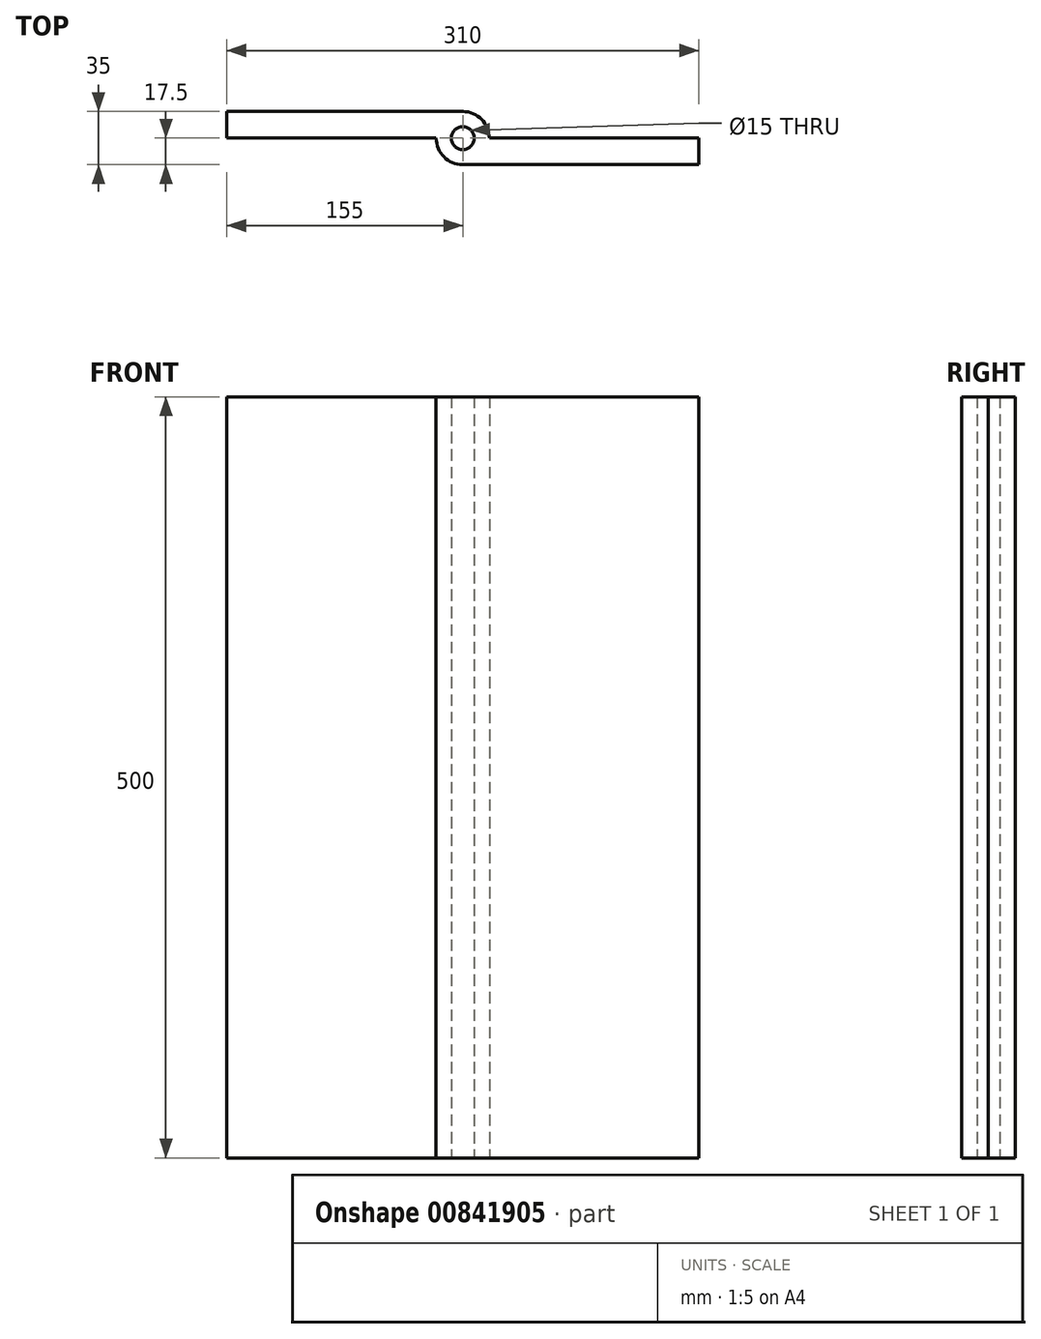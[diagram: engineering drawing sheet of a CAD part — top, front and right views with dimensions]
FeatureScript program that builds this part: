
annotation { "Feature Type Name" : "Feature", "Feature Type Description" : "" }
export const myFeature = defineFeature(function(context is Context, id is Id, definition is map)
    precondition{}
    {
        {
            var Q0;
            Q0=qCreatedBy(makeId("Top.planeOp"),FACE);
            var sketch = newSketch(context, id + "F0", { "sketchPlane" : qUnion([Q0])});
            skCircle(sketch, "E0", {"center": v(0, 0) * mm, "radius": 7.5 * mm});
            skArc(sketch, "E1.0", {"start": v(-17.5, 0) * mm, "mid": v(-12.37, -12.37) * mm, "end": v(0, -17.5) * mm});
            skLineSegment(sketch, "E2", {"start": v(17.5, 0) * mm, "end": v(155, 0) * mm});
            skLineSegment(sketch, "E3", {"start": v(0, -17.5) * mm, "end": v(155, -17.5) * mm});
            skLineSegment(sketch, "E4", {"start": v(155, 0) * mm, "end": v(155, -17.5) * mm});
            skLineSegment(sketch, "E5", {"start": v(-17.5, 0) * mm, "end": v(-155, 0) * mm});
            skLineSegment(sketch, "E6", {"start": v(0, 17.5) * mm, "end": v(-155, 17.5) * mm});
            skLineSegment(sketch, "E7", {"start": v(-155, 17.5) * mm, "end": v(-155, 0) * mm});
            skArc(sketch, "E8.trimOffspring", {"start": v(17.5, 0) * mm, "mid": v(12.37, 12.37) * mm, "end": v(0, 17.5) * mm});
            skSolve(sketch);
        }
        {
            var Q0;
            Q0=makeQuery(id+"F0.imprint","IMPRINT",FACE,{"disambiguationData":[TD([[makeQuery(id+"F0.imprint","IMPRINT",EDGE,{"derivedFrom":sQuery(id+"F0.wireOp",EDGE,"E0")}),-1.0]])]});
            extrude(context, id + "F1", {"entities" : qUnion([Q0]), "depth" : 500 * mm, "offsetDistance" : 25 * mm});
        }
        {
            var Q0;
            Q0=makeQuery(id+"F1.opExtrude","SWEPT_FACE",FACE,{"disambiguationData":[OSD([sQuery(id+"F0.wireOp",EDGE,"E3")])]});
            var sketch = newSketch(context, id + "F2", { "sketchPlane" : qUnion([Q0])});
            skLineSegment(sketch, "E9.0", {"start": v(-130, 450) * mm, "end": v(-130, 50) * mm});
            skLineSegment(sketch, "E10.0", {"start": v(130, 450) * mm, "end": v(130, 50) * mm});
            skLineSegment(sketch, "E11.0", {"start": v(-17.5, 450) * mm, "end": v(-130, 450) * mm});
            skLineSegment(sketch, "E11.1", {"start": v(-17.5, 450) * mm, "end": v(0, 450) * mm});
            skLineSegment(sketch, "E11.2", {"start": v(0, 450) * mm, "end": v(130, 450) * mm});
            skLineSegment(sketch, "E12.0", {"start": v(-17.5, 50) * mm, "end": v(-130, 50) * mm});
            skLineSegment(sketch, "E12.1", {"start": v(-17.5, 50) * mm, "end": v(0, 50) * mm});
            skLineSegment(sketch, "E12.2", {"start": v(0, 50) * mm, "end": v(130, 50) * mm});
            skSolve(sketch);
        }
        {
            var Q0;
            Q0 = qSketchRegion(id + "F2", true);
            extrude(context, id + "F3", {"entities" : qUnion([Q0]), "operationType" : NewBodyOperationType.REMOVE, "endBound" : BoundingType.UP_TO_NEXT, "oppositeDirection" : true, "depth" : 25 * mm, "offsetDistance" : 25 * mm});
        }
    });
